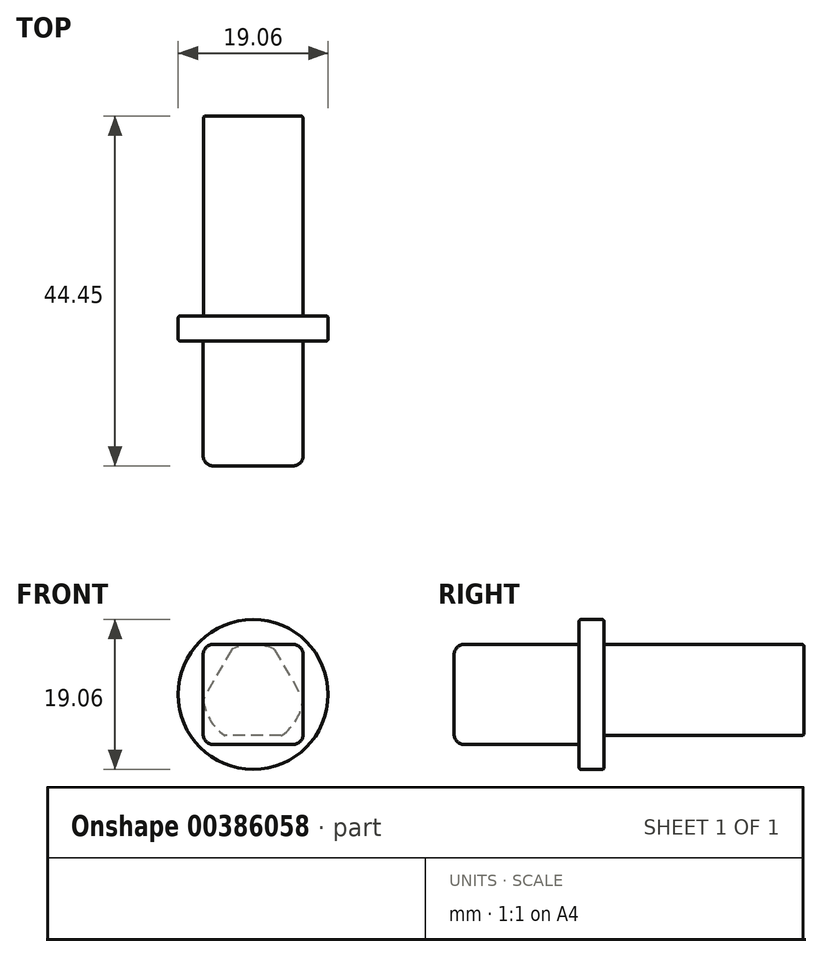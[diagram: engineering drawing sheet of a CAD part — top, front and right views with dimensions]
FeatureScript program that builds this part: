
annotation { "Feature Type Name" : "Feature", "Feature Type Description" : "" }
export const myFeature = defineFeature(function(context is Context, id is Id, definition is map)
    precondition{}
    {
        {
            var Q0;
            Q0=qCreatedBy(makeId("Front.planeOp"),FACE);
            var sketch = newSketch(context, id + "F0", { "sketchPlane" : qUnion([Q0])});
            skLineSegment(sketch, "E0.bottom", {"start": v(-6.35, 6.35) * mm, "end": v(6.35, 6.35) * mm});
            skLineSegment(sketch, "E0.top", {"start": v(-6.35, -6.35) * mm, "end": v(6.35, -6.35) * mm});
            skLineSegment(sketch, "E0.left", {"start": v(-6.35, 6.35) * mm, "end": v(-6.35, -6.35) * mm});
            skLineSegment(sketch, "E0.right", {"start": v(6.35, 6.35) * mm, "end": v(6.35, -6.35) * mm});
            skPoint(sketch, "E0.middle", {"position": v(0, 0) * mm});
            skSolve(sketch);
        }
        {
            var Q0;
            Q0=makeQuery(id+"F0.imprint","IMPRINT",FACE,{"disambiguationData":[TD([[makeQuery(id+"F0.imprint","IMPRINT",EDGE,{"derivedFrom":sQuery(id+"F0.wireOp",EDGE,"E0.bottom")}),-1.0]])]});
            extrude(context, id + "F1", {"entities" : qUnion([Q0]), "depth" : 19.05 * mm, "offsetDistance" : 25.4 * mm});
        }
        {
            var Q0;
            Q0=makeQuery(id+"F1.opExtrude","CAP_FACE",FACE,{"disambiguationData":[OSD([sQuery(id+"F0.wireOp",EDGE,"E0.bottom"),sQuery(id+"F0.wireOp",EDGE,"E0.top"),sQuery(id+"F0.wireOp",EDGE,"E0.left"),sQuery(id+"F0.wireOp",EDGE,"E0.right")])],"isStart":true});
            var sketch = newSketch(context, id + "F2", { "sketchPlane" : qUnion([Q0])});
            skCircle(sketch, "E1", {"center": v(0, 0) * mm, "radius": 9.53 * mm});
            skSolve(sketch);
        }
        {
            var Q0;
            Q0=makeQuery(id+"F2.imprint","IMPRINT",FACE,{"disambiguationData":[TD([[makeQuery(id+"F2.imprint","IMPRINT",EDGE,{"derivedFrom":sQuery(id+"F2.wireOp",EDGE,"E1")}),1.0]])]});
            extrude(context, id + "F3", {"entities" : qUnion([Q0]), "oppositeDirection" : true, "depth" : 3.17 * mm, "offsetDistance" : 25.4 * mm});
        }
        {
            var Q0;
            Q0=makeQuery(id+"F1.opExtrude","CAP_EDGE",EDGE,{"disambiguationData":[OSD([sQuery(id+"F0.wireOp",EDGE,"E0.left")])],"isStart":false});
            var Q1;
            Q1=makeQuery(id+"F1.opExtrude","CAP_FACE",FACE,{"disambiguationData":[OSD([sQuery(id+"F0.wireOp",EDGE,"E0.bottom"),sQuery(id+"F0.wireOp",EDGE,"E0.top"),sQuery(id+"F0.wireOp",EDGE,"E0.left"),sQuery(id+"F0.wireOp",EDGE,"E0.right")])],"isStart":false});
            var Q2;
            Q2=makeQuery(id+"F1.opExtrude","SWEPT_EDGE",EDGE,{"disambiguationData":[OSD([sQuery(id+"F0.wireOp",EDGE,"E0.bottom"),sQuery(id+"F0.wireOp",EDGE,"E0.left")])]});
            var Q3;
            Q3=makeQuery(id+"F1.opExtrude","SWEPT_EDGE",EDGE,{"disambiguationData":[OSD([sQuery(id+"F0.wireOp",EDGE,"E0.top"),sQuery(id+"F0.wireOp",EDGE,"E0.left")])]});
            var Q4;
            Q4=makeQuery(id+"F1.opExtrude","SWEPT_EDGE",EDGE,{"disambiguationData":[OSD([sQuery(id+"F0.wireOp",EDGE,"E0.top"),sQuery(id+"F0.wireOp",EDGE,"E0.right")])]});
            var Q5;
            Q5=makeQuery(id+"F1.opExtrude","SWEPT_EDGE",EDGE,{"disambiguationData":[OSD([sQuery(id+"F0.wireOp",EDGE,"E0.bottom"),sQuery(id+"F0.wireOp",EDGE,"E0.right")])]});
            fillet(context, id + "F4", {"entities" : qUnion([Q0, Q1, Q2, Q3, Q4, Q5]), "tangentPropagation" : true, "radius" : 1.27 * mm, "defaultsChanged" : false, "vertexSettings" : [], "allowEdgeOverflow" : false});
        }
        {
            var Q0;
            Q0=makeQuery(id+"F3.opExtrude","CAP_EDGE",EDGE,{"disambiguationData":[OSD([sQuery(id+"F2.wireOp",EDGE,"E1")])],"isStart":false});
            var Q1;
            Q1=makeQuery(id+"F3.opExtrude","CAP_EDGE",EDGE,{"disambiguationData":[OSD([sQuery(id+"F2.wireOp",EDGE,"E1")])],"isStart":true});
            fillet(context, id + "F5", {"entities" : qUnion([Q0, Q1]), "tangentPropagation" : true, "radius" : 0.25 * mm, "defaultsChanged" : false, "vertexSettings" : [], "allowEdgeOverflow" : false});
        }
        {
            var Q0;
            Q0=makeQuery(id+"F3.opExtrude","CAP_FACE",FACE,{"disambiguationData":[OSD([sQuery(id+"F0.wireOp",EDGE,"E0.bottom"),sQuery(id+"F0.wireOp",EDGE,"E0.top"),sQuery(id+"F0.wireOp",EDGE,"E0.left"),sQuery(id+"F0.wireOp",EDGE,"E0.right"),sQuery(id+"F2.wireOp",EDGE,"E1")])],"isStart":true});
            var sketch = newSketch(context, id + "F6", { "sketchPlane" : qUnion([Q0])});
            skLineSegment(sketch, "E2", {"start": v(-2.7, 5.75) * mm, "end": v(-6.33, -0.55) * mm});
            skLineSegment(sketch, "E3", {"start": v(2.7, 5.75) * mm, "end": v(6.33, -0.55) * mm});
            skLineSegment(sketch, "E4", {"start": v(-3.63, -5.2) * mm, "end": v(3.63, -5.2) * mm});
            skArc(sketch, "E5", {"start": v(-2.7, 5.75) * mm, "mid": v(0, 6.35) * mm, "end": v(2.7, 5.75) * mm});
            skArc(sketch, "E6", {"start": v(6.33, -0.55) * mm, "mid": v(5.5, -3.18) * mm, "end": v(3.63, -5.2) * mm});
            skArc(sketch, "E7", {"start": v(-3.63, -5.2) * mm, "mid": v(-5.5, -3.18) * mm, "end": v(-6.33, -0.55) * mm});
            skSolve(sketch);
        }
        {
            var Q0;
            {var subQ1=sQuery(id+"F6.wireOp",EDGE,"E2");Q0=makeQuery(id+"F6.imprint","IMPRINT",FACE,{"disambiguationData":[TD([[makeQuery(id+"F6.imprint","IMPRINT",EDGE,{"derivedFrom":subQ1}),1.0]])]});}
            extrude(context, id + "F7", {"entities" : qUnion([Q0]), "operationType" : NewBodyOperationType.ADD, "depth" : 25.4 * mm, "offsetDistance" : 25.4 * mm});
        }
        {
            var Q0;
            Q0=makeQuery(id+"F7.opExtrude","CAP_EDGE",EDGE,{"disambiguationData":[OSD([sQuery(id+"F6.wireOp",EDGE,"E2")])],"isStart":false});
            var Q1;
            Q1=makeQuery(id+"F7.opExtrude","CAP_EDGE",EDGE,{"disambiguationData":[OSD([sQuery(id+"F6.wireOp",EDGE,"E7")])],"isStart":false});
            var Q2;
            Q2=makeQuery(id+"F7.opExtrude","CAP_EDGE",EDGE,{"disambiguationData":[OSD([sQuery(id+"F6.wireOp",EDGE,"E4")])],"isStart":false});
            var Q3;
            Q3=makeQuery(id+"F7.opExtrude","CAP_EDGE",EDGE,{"disambiguationData":[OSD([sQuery(id+"F6.wireOp",EDGE,"E6")])],"isStart":false});
            var Q4;
            Q4=makeQuery(id+"F7.opExtrude","CAP_EDGE",EDGE,{"disambiguationData":[OSD([sQuery(id+"F6.wireOp",EDGE,"E3")])],"isStart":false});
            var Q5;
            Q5=makeQuery(id+"F7.opExtrude","CAP_FACE",FACE,{"disambiguationData":[OSD([sQuery(id+"F6.wireOp",EDGE,"E2"),sQuery(id+"F6.wireOp",EDGE,"E3"),sQuery(id+"F6.wireOp",EDGE,"E4"),sQuery(id+"F6.wireOp",EDGE,"E5"),sQuery(id+"F6.wireOp",EDGE,"E6"),sQuery(id+"F6.wireOp",EDGE,"E7")])],"isStart":false});
            var Q6;
            Q6=makeQuery(id+"F7.opExtrude","SWEPT_EDGE",EDGE,{"disambiguationData":[OSD([sQuery(id+"F6.wireOp",EDGE,"E2"),sQuery(id+"F6.wireOp",EDGE,"E5")])]});
            var Q7;
            Q7=makeQuery(id+"F7.opExtrude","SWEPT_EDGE",EDGE,{"disambiguationData":[OSD([sQuery(id+"F6.wireOp",EDGE,"E2"),sQuery(id+"F6.wireOp",EDGE,"E7")])]});
            var Q8;
            Q8=makeQuery(id+"F7.opExtrude","SWEPT_EDGE",EDGE,{"disambiguationData":[OSD([sQuery(id+"F6.wireOp",EDGE,"E4"),sQuery(id+"F6.wireOp",EDGE,"E7")])]});
            var Q9;
            Q9=makeQuery(id+"F7.opExtrude","SWEPT_EDGE",EDGE,{"disambiguationData":[OSD([sQuery(id+"F6.wireOp",EDGE,"E4"),sQuery(id+"F6.wireOp",EDGE,"E6")])]});
            var Q10;
            Q10=makeQuery(id+"F7.opExtrude","SWEPT_EDGE",EDGE,{"disambiguationData":[OSD([sQuery(id+"F6.wireOp",EDGE,"E3"),sQuery(id+"F6.wireOp",EDGE,"E5")])]});
            var Q11;
            Q11=makeQuery(id+"F7.opExtrude","SWEPT_EDGE",EDGE,{"disambiguationData":[OSD([sQuery(id+"F6.wireOp",EDGE,"E3"),sQuery(id+"F6.wireOp",EDGE,"E6")])]});
            fillet(context, id + "F8", {"entities" : qUnion([Q0, Q1, Q2, Q3, Q4, Q5, Q6, Q7, Q8, Q9, Q10, Q11]), "tangentPropagation" : true, "radius" : 0.25 * mm, "defaultsChanged" : false, "vertexSettings" : [], "allowEdgeOverflow" : false});
        }
        {
            var Q0;
            Q0=makeQuery(id+"F3.opExtrude","SWEPT_EDGE",EDGE,{"disambiguationData":[OSD([sQuery(id+"F0.wireOp",EDGE,"E0.bottom"),sQuery(id+"F0.wireOp",EDGE,"E0.right")])]});
            var Q1;
            Q1=makeQuery(id+"F3.opExtrude","SWEPT_EDGE",EDGE,{"disambiguationData":[OSD([sQuery(id+"F0.wireOp",EDGE,"E0.bottom"),sQuery(id+"F0.wireOp",EDGE,"E0.left")])]});
            var Q2;
            Q2=makeQuery(id+"F3.opExtrude","SWEPT_EDGE",EDGE,{"disambiguationData":[OSD([sQuery(id+"F0.wireOp",EDGE,"E0.top"),sQuery(id+"F0.wireOp",EDGE,"E0.left")])]});
            var Q3;
            Q3=makeQuery(id+"F3.opExtrude","SWEPT_EDGE",EDGE,{"disambiguationData":[OSD([sQuery(id+"F0.wireOp",EDGE,"E0.top"),sQuery(id+"F0.wireOp",EDGE,"E0.right")])]});
            fillet(context, id + "F9", {"entities" : qUnion([Q0, Q1, Q2, Q3]), "tangentPropagation" : true, "radius" : 1.27 * mm, "defaultsChanged" : false, "vertexSettings" : [], "allowEdgeOverflow" : false});
        }
    });
